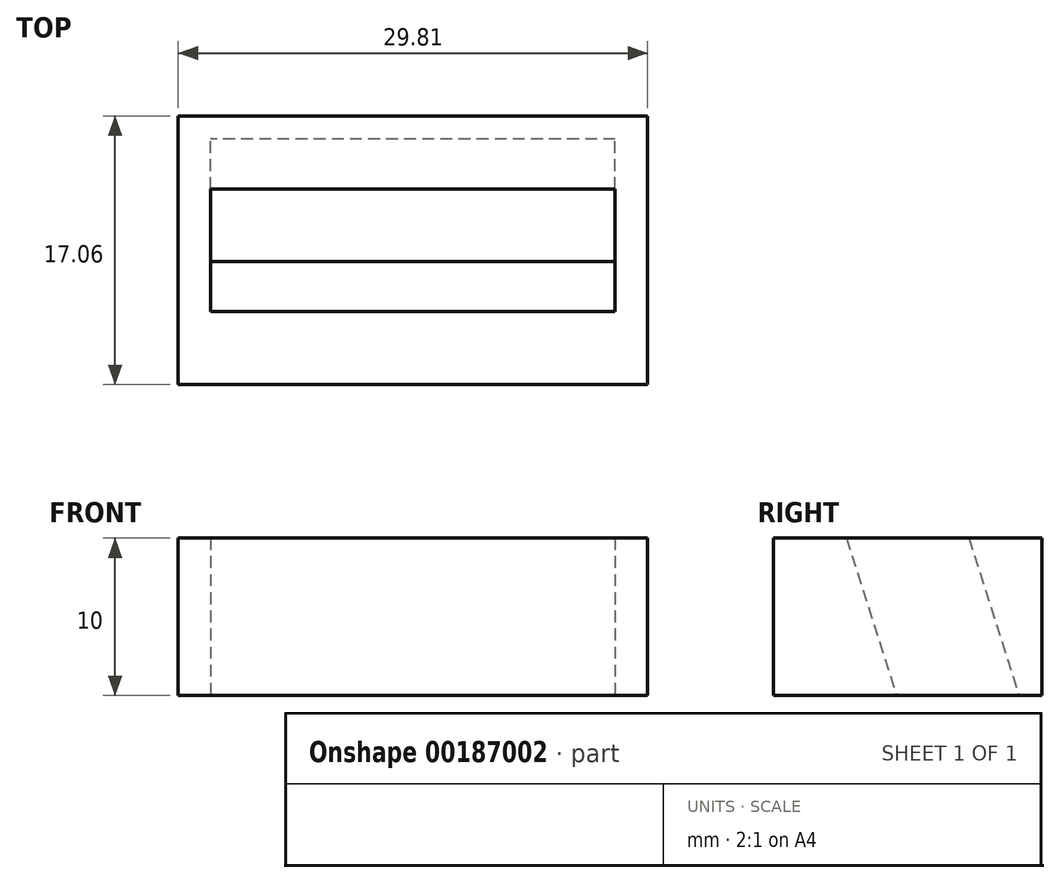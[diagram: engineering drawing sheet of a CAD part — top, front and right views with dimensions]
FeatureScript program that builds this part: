
annotation { "Feature Type Name" : "Feature", "Feature Type Description" : "" }
export const myFeature = defineFeature(function(context is Context, id is Id, definition is map)
    precondition{}
    {
        {
            var Q0;
            Q0=qCreatedBy(makeId("Top.planeOp"),FACE);
            var sketch = newSketch(context, id + "F0", { "sketchPlane" : qUnion([Q0])});
            skLineSegment(sketch, "E0.bottom", {"start": v(0, 3.3) * mm, "end": v(-29.8, 3.3) * mm});
            skLineSegment(sketch, "E0.top", {"start": v(0, 20.36) * mm, "end": v(-29.8, 20.36) * mm});
            skLineSegment(sketch, "E0.left", {"start": v(0, 3.3) * mm, "end": v(0, 20.36) * mm});
            skLineSegment(sketch, "E0.right", {"start": v(-29.8, 3.3) * mm, "end": v(-29.8, 20.36) * mm});
            skPoint(sketch, "E0.middle", {"position": v(-14.9, 11.83) * mm});
            skLineSegment(sketch, "E1.bottom", {"start": v(-2.05, 7.94) * mm, "end": v(-27.76, 7.94) * mm});
            skLineSegment(sketch, "E1.top", {"start": v(-2.05, 15.72) * mm, "end": v(-27.76, 15.72) * mm});
            skLineSegment(sketch, "E1.left", {"start": v(-2.05, 7.94) * mm, "end": v(-2.05, 15.72) * mm});
            skLineSegment(sketch, "E1.right", {"start": v(-27.76, 7.94) * mm, "end": v(-27.76, 15.72) * mm});
            skSolve(sketch);
        }
        {
            var Q0;
            Q0=makeQuery(id+"F0.imprint","IMPRINT",FACE,{"disambiguationData":[TD([[makeQuery(id+"F0.imprint","IMPRINT",EDGE,{"derivedFrom":sQuery(id+"F0.wireOp",EDGE,"E0.bottom")}),-1.0]])]});
            var Q1;
            Q1=makeQuery(id+"F0.imprint","IMPRINT",FACE,{"disambiguationData":[TD([[makeQuery(id+"F0.imprint","IMPRINT",EDGE,{"derivedFrom":sQuery(id+"F0.wireOp",EDGE,"E1.bottom")}),-1.0]])]});
            extrude(context, id + "F1", {"entities" : qUnion([Q0, Q1]), "oppositeDirection" : true, "depth" : 10 * mm});
        }
        {
            var Q0;
            Q0=makeQuery(id+"F1.opExtrude","SWEPT_FACE",FACE,{"disambiguationData":[OSD([sQuery(id+"F0.wireOp",EDGE,"E0.left")])]});
            var sketch = newSketch(context, id + "F2", { "sketchPlane" : qUnion([Q0])});
            skLineSegment(sketch, "E2", {"start": v(11.83, 0) * mm, "end": v(15, -10) * mm});
            skSolve(sketch);
        }
        {
            var Q0;
            Q0=makeQuery(id+"F0.imprint","IMPRINT",FACE,{"disambiguationData":[TD([[makeQuery(id+"F0.imprint","IMPRINT",EDGE,{"derivedFrom":sQuery(id+"F0.wireOp",EDGE,"E1.bottom")}),-1.0]])]});
            var Q1;
            Q1=sQuery(id+"F2.wireOp",EDGE,"E2");
            sweep(context, id + "F3", {"operationType" : NewBodyOperationType.REMOVE, "profiles" : qUnion([Q0]), "path" : qUnion([Q1])});
        }
    });
